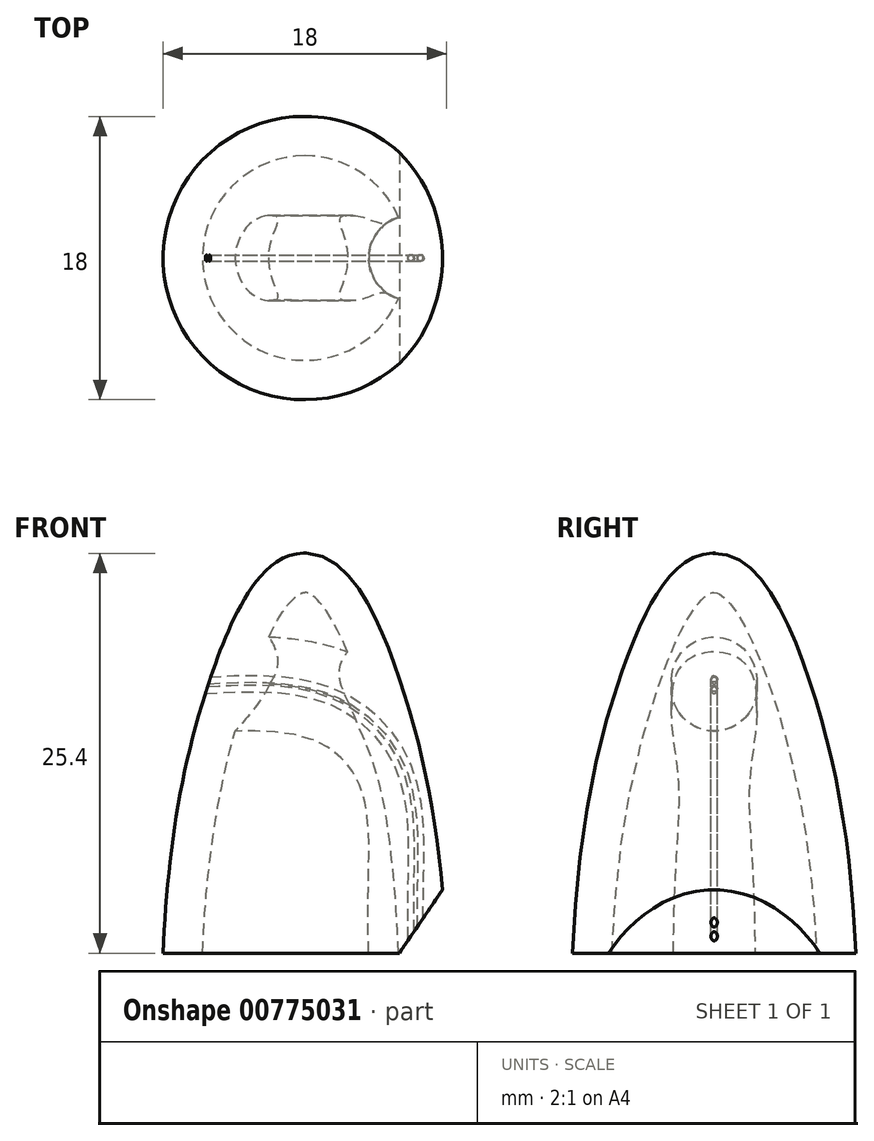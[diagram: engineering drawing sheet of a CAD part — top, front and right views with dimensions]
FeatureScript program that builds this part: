
annotation { "Feature Type Name" : "Feature", "Feature Type Description" : "" }
export const myFeature = defineFeature(function(context is Context, id is Id, definition is map)
    precondition{}
    {
        {
            var Q0;
            Q0=qCreatedBy(makeId("Right.planeOp"),FACE);
            var sketch = newSketch(context, id + "F0", { "sketchPlane" : qUnion([Q0])});
            skLineSegment(sketch, "E0", {"start": v(0, 25.4) * mm, "end": v(0, 0) * mm});
            skFitSpline(sketch, "E1", {"points": [v(0, 25.4) * mm, v(6, 17.46) * mm, v(9, 0) * mm], "startDerivative": vector(19.63, 0.61) * mm, "endDerivative": vector(1.55, -35.75) * mm});
            skLineSegment(sketch, "E2", {"start": v(9, 0) * mm, "end": v(0, 0) * mm});
            skSolve(sketch);
        }
        {
            var Q0;
            Q0=makeQuery(id+"F0.imprint","IMPRINT",FACE,{"disambiguationData":[TD([[makeQuery(id+"F0.imprint","IMPRINT",EDGE,{"derivedFrom":sQuery(id+"F0.wireOp",EDGE,"E0")}),1.0]])]});
            var Q1;
            Q1=sQuery(id+"F0.wireOp",EDGE,"E0");
            revolve(context, id + "F1", {"surfaceOperationType" : NewSurfaceOperationType.NEW, "entities" : qUnion([Q0]), "axis" : qUnion([Q1]), "revolveType" : RevolveType.FULL});
        }
        {
            var Q0;
            Q0=qCreatedBy(makeId("Front.planeOp"),FACE);
            cPlane(context, id + "F2", {"entities" : qUnion([Q0]), "cplaneType" : CPlaneType.OFFSET, "offset" : 9 * mm, "width" : 150 * mm, "height" : 150 * mm});
        }
        {
            var Q0;
            Q0=qCreatedBy(id+"F2.planeOp",FACE);
            var sketch = newSketch(context, id + "F3", { "sketchPlane" : qUnion([Q0])});
            skLineSegment(sketch, "E3", {"start": v(9, 0) * mm, "end": v(6, 0) * mm});
            skLineSegment(sketch, "E4", {"start": v(6, 0) * mm, "end": v(8.88, 4.22) * mm});
            skLineSegment(sketch, "E5", {"start": v(8.88, 4.22) * mm, "end": v(9, 0) * mm});
            skLineSegment(sketch, "E6.0", {"start": v(-9, 0) * mm, "end": v(9, 0) * mm});
            skSolve(sketch);
        }
        {
            var Q0;
            {var subQ0=sQuery(id+"F3.wireOp",EDGE,"E4");Q0=makeQuery(id+"F3.imprint","IMPRINT",FACE,{"disambiguationData":[TD([[makeQuery(id+"F3.imprint","IMPRINT",EDGE,{"derivedFrom":subQ0}),-1.0]])]});}
            extrude(context, id + "F4", {"entities" : qUnion([Q0]), "operationType" : NewBodyOperationType.REMOVE, "oppositeDirection" : true, "depth" : 25 * mm, "offsetDistance" : 25 * mm});
        }
        {
            var Q0;
            Q0=qCreatedBy(makeId("Top.planeOp"),FACE);
            cPlane(context, id + "F5", {"entities" : qUnion([Q0]), "cplaneType" : CPlaneType.OFFSET, "offset" : 0 * mm, "width" : 150 * mm, "height" : 150 * mm});
        }
        {
            var Q0;
            Q0=qCreatedBy(id+"F5.planeOp",FACE);
            var sketch = newSketch(context, id + "F6", { "sketchPlane" : qUnion([Q0])});
            skCircle(sketch, "E7", {"center": v(6.74, 0) * mm, "radius": 0.2 * mm});
            skPoint(sketch, "E8.0", {"position": v(8.74, 0) * mm});
            skPoint(sketch, "E9.0", {"position": v(6, 0) * mm});
            skCircle(sketch, "E10", {"center": v(7.34, 0) * mm, "radius": 0.2 * mm});
            skSolve(sketch);
        }
        {
            var Q0;
            Q0=qCreatedBy(makeId("Front.planeOp"),FACE);
            cPlane(context, id + "F7", {"entities" : qUnion([Q0]), "cplaneType" : CPlaneType.OFFSET, "offset" : 0 * mm, "width" : 150 * mm, "height" : 150 * mm});
        }
        {
            var Q0;
            Q0=qCreatedBy(id+"F7.planeOp",FACE);
            var sketch = newSketch(context, id + "F8", { "sketchPlane" : qUnion([Q0])});
            skPoint(sketch, "E11.0", {"position": v(7.34, 0) * mm});
            skPoint(sketch, "E12.0", {"position": v(6.74, 0) * mm});
            skFitSpline(sketch, "E13", {"points": [v(7.34, 0) * mm, v(6.81, 12.03) * mm, v(1.94, 16.94) * mm, v(-4.11, 17.55) * mm, v(-6.9, 17.28) * mm], "startDerivative": vector(2.72, 39.19) * mm, "endDerivative": vector(-15.16, -1.86) * mm});
            skFitSpline(sketch, "E14", {"points": [v(6.74, 0) * mm, v(6.74, 4.51) * mm, v(6.06, 11.52) * mm, v(1.6, 16.02) * mm, v(-4.25, 16.8) * mm, v(-7.07, 16.63) * mm], "startDerivative": vector(-0.18, 22.45) * mm, "endDerivative": vector(-17.13, -1.42) * mm});
            skSolve(sketch);
        }
        {
            var Q0;
            Q0=makeQuery(id+"F6.imprint","IMPRINT",FACE,{"disambiguationData":[TD([[makeQuery(id+"F6.imprint","IMPRINT",EDGE,{"derivedFrom":sQuery(id+"F6.wireOp",EDGE,"E7")}),1.0]])]});
            var Q1;
            Q1=makeQuery(id+"F6.imprint","IMPRINT",FACE,{"disambiguationData":[TD([[makeQuery(id+"F6.imprint","IMPRINT",EDGE,{"derivedFrom":sQuery(id+"F6.wireOp",EDGE,"E10")}),1.0]])]});
            var Q2;
            Q2=sQuery(id+"F8.wireOp",EDGE,"E14");
            sweep(context, id + "F9", {"operationType" : NewBodyOperationType.REMOVE, "profiles" : qUnion([Q0, Q1]), "path" : qUnion([Q2])});
        }
        {
            var Q0;
            Q0=makeQuery(id+"F1.opRevolve","SWEPT_FACE",FACE,{"disambiguationData":[OSD([sQuery(id+"F0.wireOp",EDGE,"E2")])]});
            var Q1;
            Q1=makeQuery(id+"F4.boolean.opBoolean","COPY",FACE,{"derivedFrom":makeQuery(id+"F4.opExtrude","SWEPT_FACE",FACE,{"disambiguationData":[OSD([sQuery(id+"F3.wireOp",EDGE,"E4")])]})});
            shell(context, id + "F10", {"entities" : qUnion([Q0, Q1]), "thickness" : 2.5 * mm});
        }
    });
